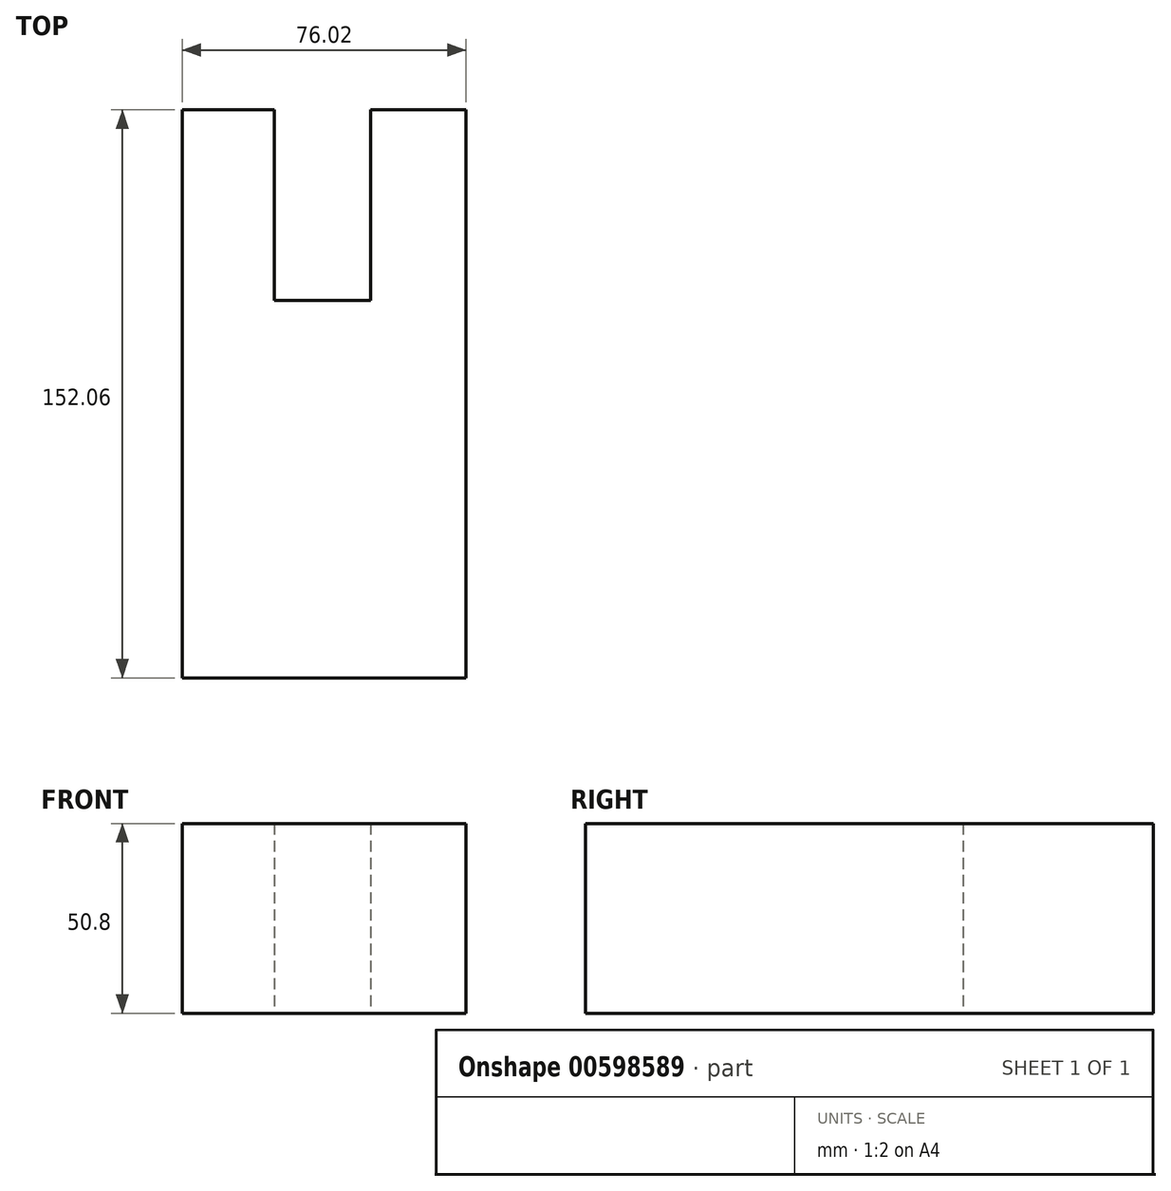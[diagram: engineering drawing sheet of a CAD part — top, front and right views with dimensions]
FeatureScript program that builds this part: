
annotation { "Feature Type Name" : "Feature", "Feature Type Description" : "" }
export const myFeature = defineFeature(function(context is Context, id is Id, definition is map)
    precondition{}
    {
        {
            var Q0;
            Q0=qCreatedBy(makeId("Top.planeOp"),FACE);
            var sketch = newSketch(context, id + "F0", { "sketchPlane" : qUnion([Q0])});
            skLineSegment(sketch, "E0", {"start": v(0, 0) * mm, "end": v(0, -152.06) * mm});
            skLineSegment(sketch, "E1", {"start": v(0, -152.06) * mm, "end": v(76.02, -152.06) * mm});
            skLineSegment(sketch, "E2", {"start": v(76.02, -152.06) * mm, "end": v(76.02, 0) * mm});
            skLineSegment(sketch, "E3", {"start": v(76.02, 0) * mm, "end": v(50.45, 0) * mm});
            skLineSegment(sketch, "E4", {"start": v(50.45, 0) * mm, "end": v(50.45, -50.97) * mm});
            skLineSegment(sketch, "E5", {"start": v(50.45, -50.97) * mm, "end": v(24.75, -50.97) * mm});
            skLineSegment(sketch, "E6", {"start": v(24.75, -50.97) * mm, "end": v(24.75, 0) * mm});
            skLineSegment(sketch, "E7", {"start": v(24.75, 0) * mm, "end": v(0, 0) * mm});
            skSolve(sketch);
        }
        {
            var Q0;
            Q0=makeQuery(id+"F0.imprint","IMPRINT",FACE,{"disambiguationData":[TD([[makeQuery(id+"F0.imprint","IMPRINT",EDGE,{"derivedFrom":sQuery(id+"F0.wireOp",EDGE,"E0")}),1.0]])]});
            extrude(context, id + "F1", {"entities" : qUnion([Q0]), "depth" : 50.8 * mm, "offsetDistance" : 25.4 * mm});
        }
    });
